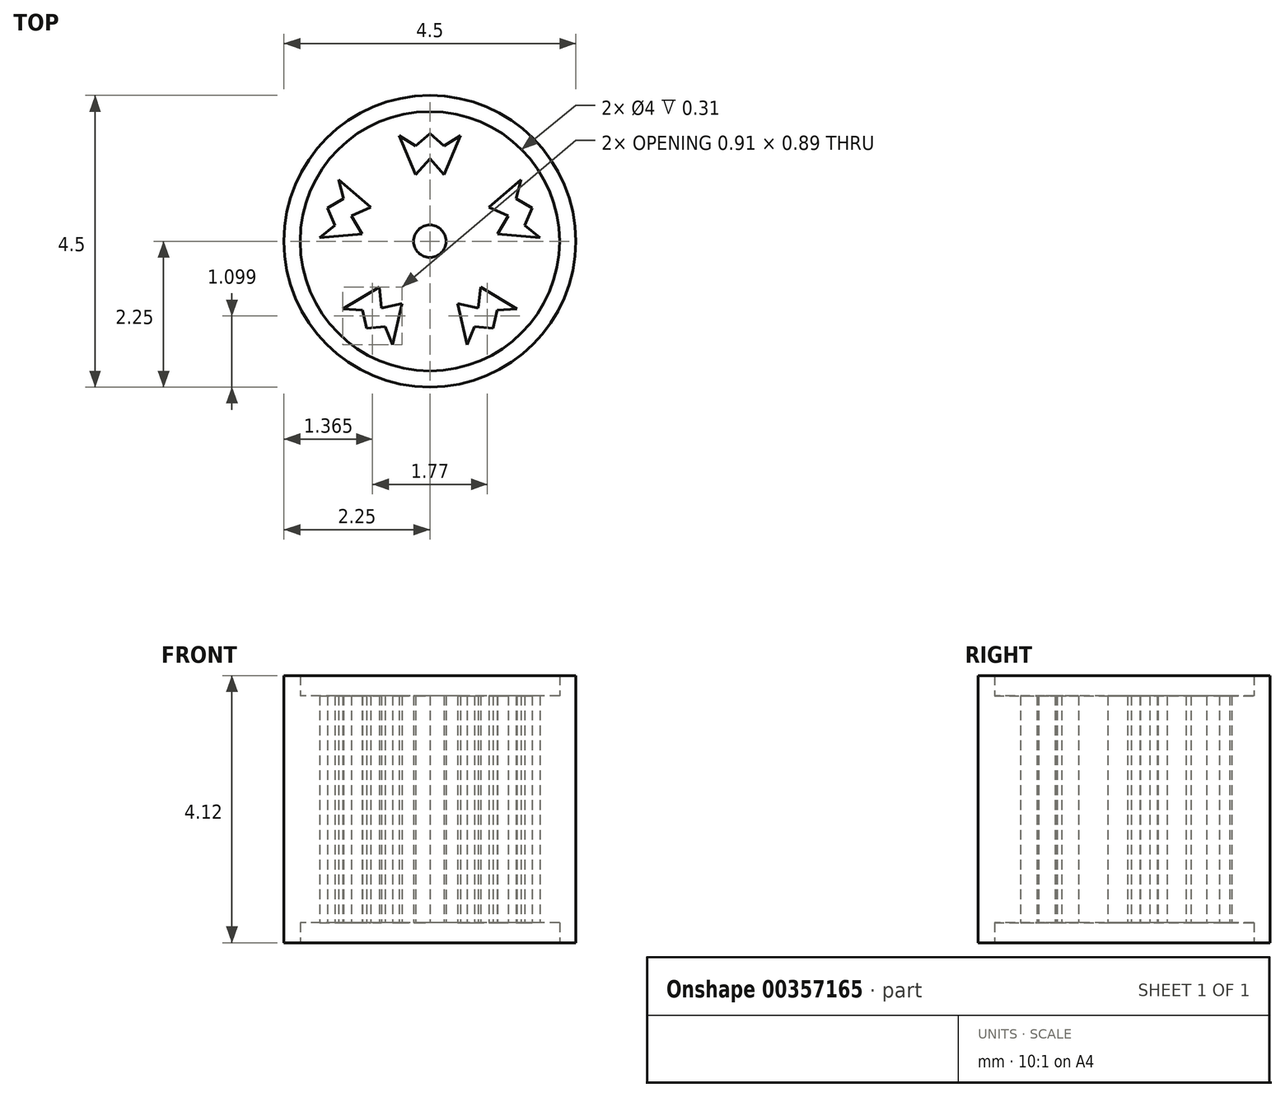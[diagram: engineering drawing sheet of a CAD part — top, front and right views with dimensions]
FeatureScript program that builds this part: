
annotation { "Feature Type Name" : "Feature", "Feature Type Description" : "" }
export const myFeature = defineFeature(function(context is Context, id is Id, definition is map)
    precondition{}
    {
        {
            var Q0;
            Q0=qCreatedBy(makeId("Top.planeOp"),FACE);
            var sketch = newSketch(context, id + "F0", { "sketchPlane" : qUnion([Q0])});
            skCircle(sketch, "E0", {"center": v(0, 0) * mm, "radius": 0.25 * mm});
            skCircle(sketch, "E1", {"center": v(0, 0) * mm, "radius": 2.25 * mm});
            skCircle(sketch, "E2", {"center": v(0, 0) * mm, "radius": 2 * mm});
            skLineSegment(sketch, "E3", {"start": v(-0.47, 1.63) * mm, "end": v(-0.22, 1.03) * mm});
            skLineSegment(sketch, "E4", {"start": v(-0.22, 1.03) * mm, "end": v(0, 1.27) * mm});
            skLineSegment(sketch, "E5", {"start": v(-0.47, 1.63) * mm, "end": v(-0.22, 1.47) * mm});
            skLineSegment(sketch, "E6", {"start": v(-0.22, 1.47) * mm, "end": v(0, 1.66) * mm});
            skLineSegment(sketch, "E7.MirrorCS", {"start": v(0.22, 1.47) * mm, "end": v(0, 1.66) * mm});
            skLineSegment(sketch, "E8.MirrorCS", {"start": v(0.47, 1.63) * mm, "end": v(0.22, 1.47) * mm});
            skLineSegment(sketch, "E9.MirrorCS", {"start": v(0.47, 1.63) * mm, "end": v(0.22, 1.03) * mm});
            skLineSegment(sketch, "E10.MirrorCS", {"start": v(0.22, 1.03) * mm, "end": v(0, 1.27) * mm});
            skLineSegment(sketch, "E11.1.0", {"start": v(-1.33, 0.66) * mm, "end": v(-1.58, 0.51) * mm});
            skLineSegment(sketch, "E11.1.1", {"start": v(-1.46, 0.25) * mm, "end": v(-1.58, 0.51) * mm});
            skLineSegment(sketch, "E11.1.2", {"start": v(-1.7, 0.05) * mm, "end": v(-1.46, 0.25) * mm});
            skLineSegment(sketch, "E11.1.3", {"start": v(-1.7, 0.05) * mm, "end": v(-1.05, 0.11) * mm});
            skLineSegment(sketch, "E11.1.4", {"start": v(-1.05, 0.11) * mm, "end": v(-1.21, 0.4) * mm});
            skLineSegment(sketch, "E11.1.5", {"start": v(-0.91, 0.53) * mm, "end": v(-1.21, 0.4) * mm});
            skLineSegment(sketch, "E11.1.6", {"start": v(-1.4, 0.95) * mm, "end": v(-0.91, 0.53) * mm});
            skLineSegment(sketch, "E11.1.7", {"start": v(-1.4, 0.95) * mm, "end": v(-1.33, 0.66) * mm});
            skLineSegment(sketch, "E11.2.0", {"start": v(-1.04, -1.06) * mm, "end": v(-0.98, -1.34) * mm});
            skLineSegment(sketch, "E11.2.1", {"start": v(-0.69, -1.32) * mm, "end": v(-0.98, -1.34) * mm});
            skLineSegment(sketch, "E11.2.2", {"start": v(-0.58, -1.6) * mm, "end": v(-0.69, -1.32) * mm});
            skLineSegment(sketch, "E11.2.3", {"start": v(-0.58, -1.6) * mm, "end": v(-0.43, -0.96) * mm});
            skLineSegment(sketch, "E11.2.4", {"start": v(-0.43, -0.96) * mm, "end": v(-0.75, -1.03) * mm});
            skLineSegment(sketch, "E11.2.5", {"start": v(-0.78, -0.7) * mm, "end": v(-0.75, -1.03) * mm});
            skLineSegment(sketch, "E11.2.6", {"start": v(-1.34, -1.04) * mm, "end": v(-0.78, -0.7) * mm});
            skLineSegment(sketch, "E11.2.7", {"start": v(-1.34, -1.04) * mm, "end": v(-1.04, -1.06) * mm});
            skLineSegment(sketch, "E11.3.0", {"start": v(0.69, -1.32) * mm, "end": v(0.98, -1.34) * mm});
            skLineSegment(sketch, "E11.3.1", {"start": v(1.04, -1.06) * mm, "end": v(0.98, -1.34) * mm});
            skLineSegment(sketch, "E11.3.2", {"start": v(1.34, -1.04) * mm, "end": v(1.04, -1.06) * mm});
            skLineSegment(sketch, "E11.3.3", {"start": v(1.34, -1.04) * mm, "end": v(0.78, -0.7) * mm});
            skLineSegment(sketch, "E11.3.4", {"start": v(0.78, -0.7) * mm, "end": v(0.75, -1.03) * mm});
            skLineSegment(sketch, "E11.3.5", {"start": v(0.43, -0.96) * mm, "end": v(0.75, -1.03) * mm});
            skLineSegment(sketch, "E11.3.6", {"start": v(0.58, -1.6) * mm, "end": v(0.43, -0.96) * mm});
            skLineSegment(sketch, "E11.3.7", {"start": v(0.58, -1.6) * mm, "end": v(0.69, -1.32) * mm});
            skLineSegment(sketch, "E11.4.0", {"start": v(1.46, 0.25) * mm, "end": v(1.58, 0.51) * mm});
            skLineSegment(sketch, "E11.4.1", {"start": v(1.33, 0.66) * mm, "end": v(1.58, 0.51) * mm});
            skLineSegment(sketch, "E11.4.2", {"start": v(1.4, 0.95) * mm, "end": v(1.33, 0.66) * mm});
            skLineSegment(sketch, "E11.4.3", {"start": v(1.4, 0.95) * mm, "end": v(0.91, 0.53) * mm});
            skLineSegment(sketch, "E11.4.4", {"start": v(0.91, 0.53) * mm, "end": v(1.21, 0.4) * mm});
            skLineSegment(sketch, "E11.4.5", {"start": v(1.05, 0.11) * mm, "end": v(1.21, 0.4) * mm});
            skLineSegment(sketch, "E11.4.6", {"start": v(1.7, 0.05) * mm, "end": v(1.05, 0.11) * mm});
            skLineSegment(sketch, "E11.4.7", {"start": v(1.7, 0.05) * mm, "end": v(1.46, 0.25) * mm});
            skSolve(sketch);
        }
        {
            var Q0;
            Q0=makeQuery(id+"F0.imprint","IMPRINT",FACE,{"disambiguationData":[TD([[makeQuery(id+"F0.imprint","IMPRINT",EDGE,{"derivedFrom":sQuery(id+"F0.wireOp",EDGE,"E0")}),-1.0]])]});
            extrude(context, id + "F1", {"entities" : qUnion([Q0]), "endBound" : BoundingType.SYMMETRIC, "depth" : 3.5 * mm});
        }
        {
            var Q0;
            Q0=makeQuery(id+"F0.imprint","IMPRINT",FACE,{"disambiguationData":[TD([[makeQuery(id+"F0.imprint","IMPRINT",EDGE,{"derivedFrom":sQuery(id+"F0.wireOp",EDGE,"E1")}),1.0]])]});
            extrude(context, id + "F2", {"entities" : qUnion([Q0]), "operationType" : NewBodyOperationType.ADD, "endBound" : BoundingType.SYMMETRIC, "depth" : 4.12 * mm});
        }
    });
